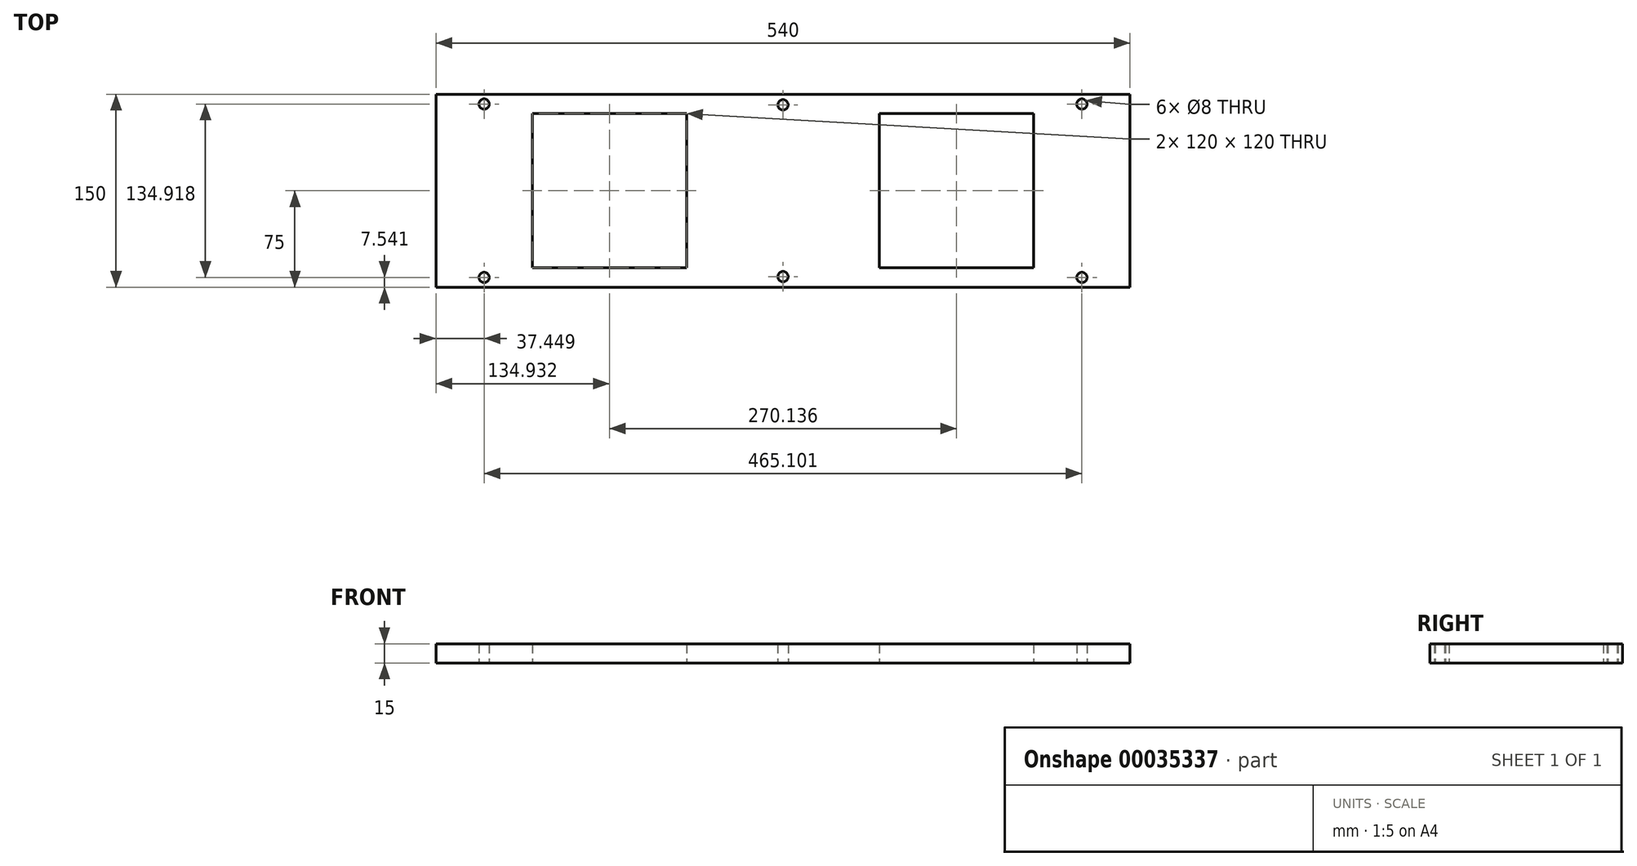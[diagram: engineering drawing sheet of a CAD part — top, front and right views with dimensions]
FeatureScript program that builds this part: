
annotation { "Feature Type Name" : "Feature", "Feature Type Description" : "" }
export const myFeature = defineFeature(function(context is Context, id is Id, definition is map)
    precondition{}
    {
        {
            var Q0;
            Q0=qCreatedBy(makeId("Top.planeOp"),FACE);
            var sketch = newSketch(context, id + "F0", { "sketchPlane" : qUnion([Q0])});
            skLineSegment(sketch, "E0", {"start": v(0, 0) * mm, "end": v(0, -150) * mm});
            skLineSegment(sketch, "E1", {"start": v(0, -150) * mm, "end": v(540, -150) * mm});
            skLineSegment(sketch, "E2", {"start": v(540, -150) * mm, "end": v(540, 0) * mm});
            skLineSegment(sketch, "E3", {"start": v(540, 0) * mm, "end": v(0, 0) * mm});
            skLineSegment(sketch, "E4", {"start": v(270, 0) * mm, "end": v(270, -150) * mm, "construction": true});
            skLineSegment(sketch, "E5.bottom", {"start": v(74.93, -15) * mm, "end": v(194.93, -15) * mm});
            skLineSegment(sketch, "E5.top", {"start": v(74.93, -135) * mm, "end": v(194.93, -135) * mm});
            skLineSegment(sketch, "E5.left", {"start": v(74.93, -15) * mm, "end": v(74.93, -135) * mm});
            skLineSegment(sketch, "E5.right", {"start": v(194.93, -15) * mm, "end": v(194.93, -135) * mm});
            skLineSegment(sketch, "E6.MirrorCS", {"start": v(465.07, -135) * mm, "end": v(345.07, -135) * mm});
            skLineSegment(sketch, "E7.MirrorCS", {"start": v(345.07, -15) * mm, "end": v(345.07, -135) * mm});
            skLineSegment(sketch, "E8.MirrorCS", {"start": v(465.07, -15) * mm, "end": v(345.07, -15) * mm});
            skLineSegment(sketch, "E9.MirrorCS", {"start": v(465.07, -15) * mm, "end": v(465.07, -135) * mm});
            skCircle(sketch, "E10", {"center": v(270, -8.17) * mm, "radius": 4 * mm});
            skLineSegment(sketch, "E11", {"start": v(0, -75) * mm, "end": v(540, -75) * mm, "construction": true});
            skCircle(sketch, "E12.MirrorC", {"center": v(270, -141.83) * mm, "radius": 4 * mm});
            skPoint(sketch, "E13.startSnap0", {"position": v(134.93, -135) * mm});
            skPoint(sketch, "E13.endSnap0", {"position": v(134.93, -15) * mm});
            skCircle(sketch, "E14", {"center": v(37.45, -7.54) * mm, "radius": 4 * mm});
            skCircle(sketch, "E15.MirrorC", {"center": v(37.45, -142.46) * mm, "radius": 4 * mm});
            skCircle(sketch, "E16.MirrorC", {"center": v(502.55, -7.54) * mm, "radius": 4 * mm});
            skCircle(sketch, "E17.MirrorC", {"center": v(502.55, -142.46) * mm, "radius": 4 * mm});
            skSolve(sketch);
        }
        {
            var Q0;
            Q0=makeQuery(id+"F0.imprint","IMPRINT",FACE,{"disambiguationData":[TD([[makeQuery(id+"F0.imprint","IMPRINT",EDGE,{"derivedFrom":sQuery(id+"F0.wireOp",EDGE,"E0")}),1.0]])]});
            extrude(context, id + "F1", {"entities" : qUnion([Q0]), "depth" : 15 * mm});
        }
    });
